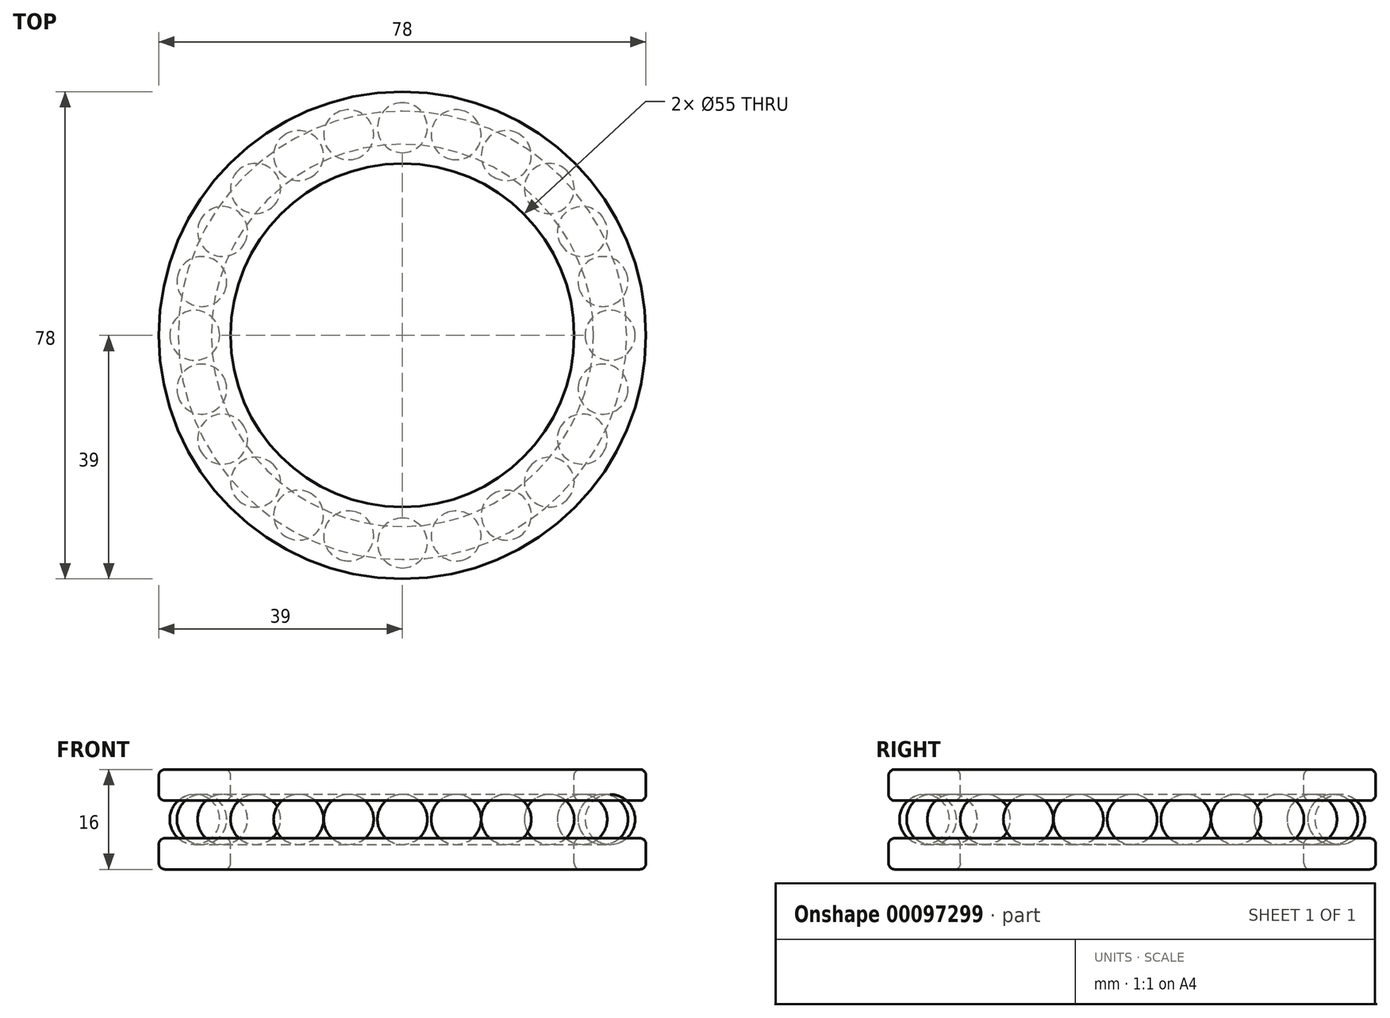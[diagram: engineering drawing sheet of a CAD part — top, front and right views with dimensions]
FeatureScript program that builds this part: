
annotation { "Feature Type Name" : "Feature", "Feature Type Description" : "" }
export const myFeature = defineFeature(function(context is Context, id is Id, definition is map)
    precondition{}
    {
        {
            var Q0;
            Q0=qCreatedBy(makeId("Front.planeOp"),FACE);
            var sketch = newSketch(context, id + "F0", { "sketchPlane" : qUnion([Q0])});
            skLineSegment(sketch, "E0", {"start": v(-39, -8) * mm, "end": v(-27.5, -8) * mm});
            skLineSegment(sketch, "E1", {"start": v(-27.5, -8) * mm, "end": v(-27.5, -3) * mm});
            skLineSegment(sketch, "E2", {"start": v(-27.5, -3) * mm, "end": v(-30.6, -3) * mm});
            skLineSegment(sketch, "E3", {"start": v(-39, -8) * mm, "end": v(-39, -3) * mm});
            skLineSegment(sketch, "E4", {"start": v(-39, -3) * mm, "end": v(-35.9, -3) * mm});
            skArc(sketch, "E5", {"start": v(-35.9, -3) * mm, "mid": v(-33.25, -4) * mm, "end": v(-30.6, -3) * mm});
            skLineSegment(sketch, "E6", {"start": v(-39, 0) * mm, "end": v(-27.5, 0) * mm});
            skLineSegment(sketch, "E7.MirrorCS", {"start": v(-39, 3) * mm, "end": v(-35.9, 3) * mm});
            skArc(sketch, "E8.MirrorCS", {"start": v(-35.9, 3) * mm, "mid": v(-33.25, 4) * mm, "end": v(-30.6, 3) * mm});
            skLineSegment(sketch, "E9.MirrorCS", {"start": v(-27.5, 3) * mm, "end": v(-30.6, 3) * mm});
            skLineSegment(sketch, "E10.MirrorCS", {"start": v(-27.5, 8) * mm, "end": v(-27.5, 3) * mm});
            skLineSegment(sketch, "E11.MirrorCS", {"start": v(-39, 8) * mm, "end": v(-27.5, 8) * mm});
            skLineSegment(sketch, "E12.MirrorCS", {"start": v(-39, 8) * mm, "end": v(-39, 3) * mm});
            skLineSegment(sketch, "E13", {"start": v(0, 8) * mm, "end": v(0, -8) * mm, "construction": true});
            skArc(sketch, "E14", {"start": v(-37.25, 0) * mm, "mid": v(-33.25, -4) * mm, "end": v(-29.25, 0) * mm});
            skArc(sketch, "E15", {"start": v(-29.25, 0) * mm, "mid": v(-33.25, 4) * mm, "end": v(-37.25, 0) * mm});
            skSolve(sketch);
        }
        {
            var Q0;
            Q0=makeQuery(id+"F0.imprint","IMPRINT",FACE,{"disambiguationData":[TD([[makeQuery(id+"F0.imprint","IMPRINT",EDGE,{"derivedFrom":sQuery(id+"F0.wireOp",EDGE,"E7.MirrorCS")}),1.0]])]});
            var Q1;
            Q1=makeQuery(id+"F0.imprint","IMPRINT",FACE,{"disambiguationData":[TD([[makeQuery(id+"F0.imprint","IMPRINT",EDGE,{"derivedFrom":sQuery(id+"F0.wireOp",EDGE,"E0")}),1.0]])]});
            var Q2;
            Q2=sQuery(id+"F0.wireOp",EDGE,"E13");
            revolve(context, id + "F1", {"surfaceOperationType" : NewSurfaceOperationType.NEW, "entities" : qUnion([Q0, Q1]), "axis" : qUnion([Q2]), "revolveType" : RevolveType.FULL});
        }
        {
            var Q0;
            {var subQ0=sQuery(id+"F0.wireOp",EDGE,"E5");Q0=makeQuery(id+"F0.imprint","IMPRINT",FACE,{"disambiguationData":[TD([[makeQuery(id+"F0.imprint","IMPRINT",EDGE,{"derivedFrom":subQ0}),1.0]])]});}
            var Q1;
            Q1=sQuery(id+"F0.wireOp",EDGE,"E6");
            revolve(context, id + "F2", {"surfaceOperationType" : NewSurfaceOperationType.NEW, "entities" : qUnion([Q0]), "axis" : qUnion([Q1]), "revolveType" : RevolveType.FULL});
        }
        {
            var Q0;
            Q0=makeQuery(id+"F2.opRevolve","SWEPT_BODY",BODY,{"disambiguationData":[OSD([sQuery(id+"F0.wireOp",EDGE,"E5"),sQuery(id+"F0.wireOp",EDGE,"E6"),sQuery(id+"F0.wireOp",EDGE,"E14")])]});
            var Q1;
            Q1=sQuery(id+"F0.wireOp",EDGE,"E13");
            circularPattern(context, id + "F3", {"entities" : qUnion([Q0]), "axis" : qUnion([Q1]), "angle" : 360 * degree, "instanceCount" : 24, "equalSpace" : true});
        }
        {
            var Q0;
            Q0=makeQuery(id+"F1.opRevolve","SWEPT_EDGE",EDGE,{"disambiguationData":[OSD([sQuery(id+"F0.wireOp",EDGE,"E11.MirrorCS"),sQuery(id+"F0.wireOp",EDGE,"E12.MirrorCS")])]});
            var Q1;
            Q1=makeQuery(id+"F1.opRevolve","SWEPT_EDGE",EDGE,{"disambiguationData":[OSD([sQuery(id+"F0.wireOp",EDGE,"E0"),sQuery(id+"F0.wireOp",EDGE,"E3")])]});
            var Q2;
            Q2=makeQuery(id+"F1.opRevolve","SWEPT_EDGE",EDGE,{"disambiguationData":[OSD([sQuery(id+"F0.wireOp",EDGE,"E3"),sQuery(id+"F0.wireOp",EDGE,"E4")])]});
            var Q3;
            Q3=makeQuery(id+"F1.opRevolve","SWEPT_EDGE",EDGE,{"disambiguationData":[OSD([sQuery(id+"F0.wireOp",EDGE,"E7.MirrorCS"),sQuery(id+"F0.wireOp",EDGE,"E12.MirrorCS")])]});
            var Q4;
            Q4=makeQuery(id+"F1.opRevolve","SWEPT_EDGE",EDGE,{"disambiguationData":[OSD([sQuery(id+"F0.wireOp",EDGE,"E0"),sQuery(id+"F0.wireOp",EDGE,"E1")])]});
            var Q5;
            Q5=makeQuery(id+"F1.opRevolve","SWEPT_EDGE",EDGE,{"disambiguationData":[OSD([sQuery(id+"F0.wireOp",EDGE,"E1"),sQuery(id+"F0.wireOp",EDGE,"E2")])]});
            var Q6;
            Q6=makeQuery(id+"F1.opRevolve","SWEPT_EDGE",EDGE,{"disambiguationData":[OSD([sQuery(id+"F0.wireOp",EDGE,"E9.MirrorCS"),sQuery(id+"F0.wireOp",EDGE,"E10.MirrorCS")])]});
            var Q7;
            Q7=makeQuery(id+"F1.opRevolve","SWEPT_EDGE",EDGE,{"disambiguationData":[OSD([sQuery(id+"F0.wireOp",EDGE,"E10.MirrorCS"),sQuery(id+"F0.wireOp",EDGE,"E11.MirrorCS")])]});
            fillet(context, id + "F4", {"entities" : qUnion([Q0, Q1, Q2, Q3, Q4, Q5, Q6, Q7]), "radius" : 1 * mm, "tangentPropagation" : true, "allowEdgeOverflow" : false});
        }
    });
